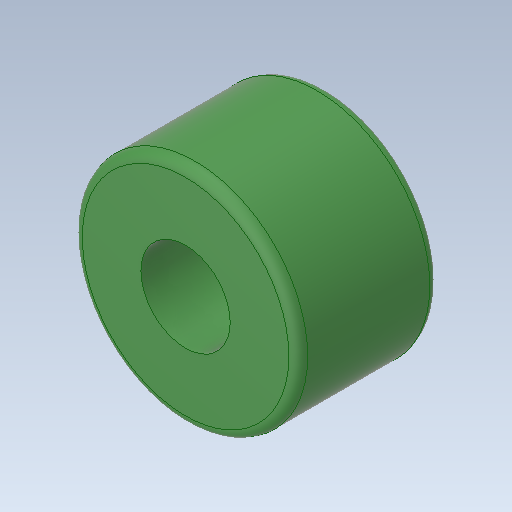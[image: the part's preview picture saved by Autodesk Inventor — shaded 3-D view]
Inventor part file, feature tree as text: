
AUTODESK INVENTOR PART (.ipt)
format: ipt  version: 2020.1 (Build 241239000, 239)  size: 141,312 bytes
history: native  units: mm
features: other x1, extrude x1, fillet x1, sketch x1
ambient origin geometry x8: Origin, YZ Plane, XZ Plane, XY Plane, X Axis, Y Axis, Z Axis, Center Point
bodies: Body1 (feature_tree)
feature tree (4):
  other  "Твердое тело1"
  extrude  "Выдавливание1"  Depth=24.0mm
  fillet  "Сопряжение1"  Radius=9.5mm
  sketch  "Эскиз1"
